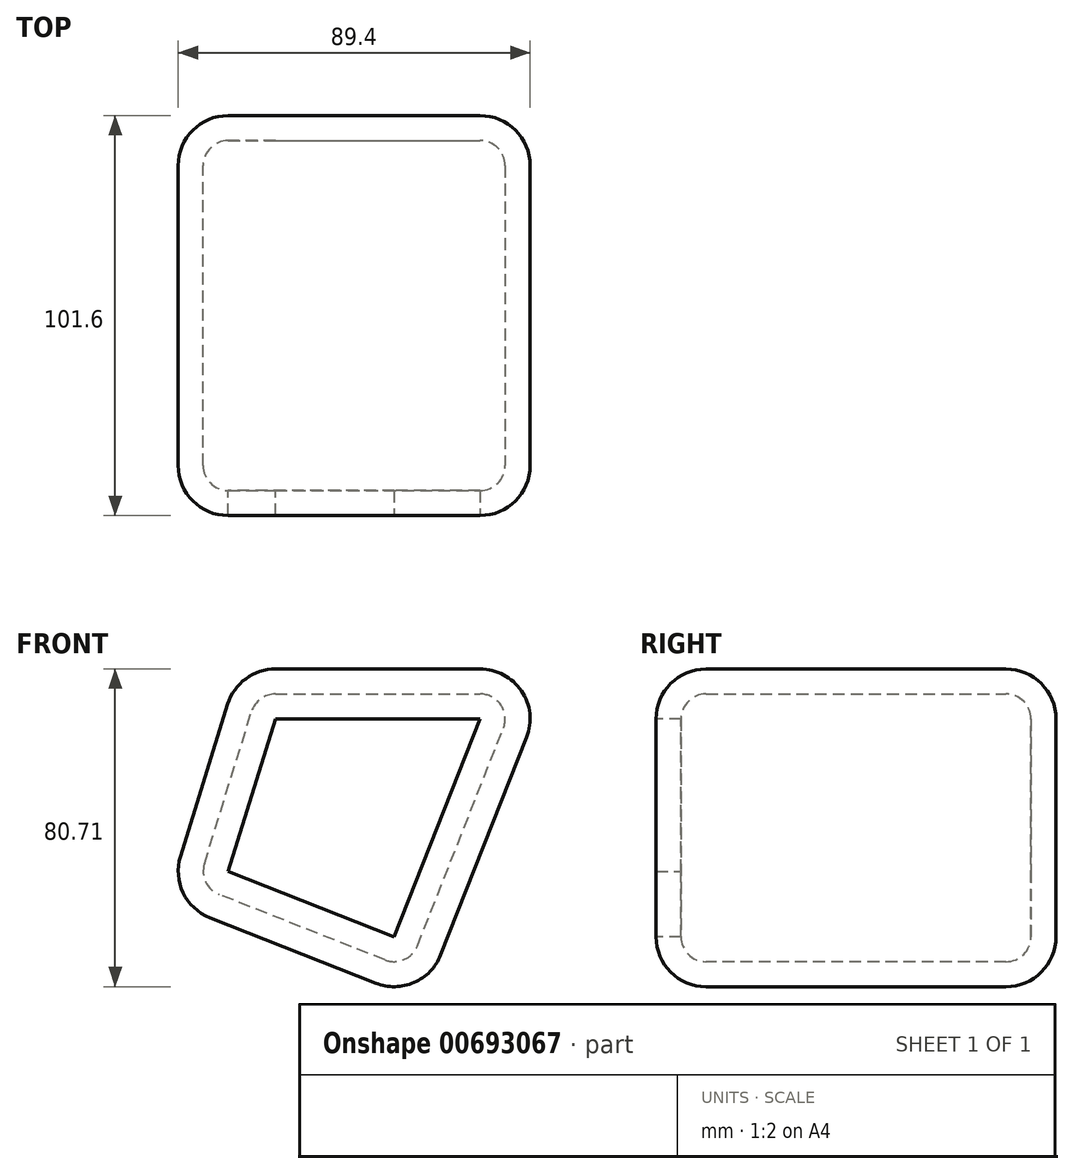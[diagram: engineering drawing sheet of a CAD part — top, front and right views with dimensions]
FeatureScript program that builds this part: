
annotation { "Feature Type Name" : "Feature", "Feature Type Description" : "" }
export const myFeature = defineFeature(function(context is Context, id is Id, definition is map)
    precondition{}
    {
        {
            var Q0;
            Q0=qCreatedBy(makeId("Front.planeOp"),FACE);
            var sketch = newSketch(context, id + "F0", { "sketchPlane" : qUnion([Q0])});
            skLineSegment(sketch, "E0", {"start": v(-44.02, 21.6) * mm, "end": v(36, 21.6) * mm});
            skLineSegment(sketch, "E1", {"start": v(36, 21.6) * mm, "end": v(36, 21.6) * mm});
            skLineSegment(sketch, "E2", {"start": v(2.64, -62.88) * mm, "end": v(36, 21.6) * mm});
            skLineSegment(sketch, "E3", {"start": v(2.64, -62.88) * mm, "end": v(-62.3, -37.23) * mm});
            skLineSegment(sketch, "E4", {"start": v(-62.3, -37.23) * mm, "end": v(-44.02, 21.6) * mm});
            skSolve(sketch);
        }
        {
            var Q0;
            Q0=makeQuery(id+"F0.imprint","IMPRINT",FACE,{"disambiguationData":[TD([[makeQuery(id+"F0.imprint","IMPRINT",EDGE,{"derivedFrom":sQuery(id+"F0.wireOp",EDGE,"E0")}),-1.0]])]});
            extrude(context, id + "F1", {"entities" : qUnion([Q0]), "endBound" : BoundingType.SYMMETRIC, "depth" : 101.6 * mm, "offsetDistance" : 25.4 * mm});
        }
        {
            var Q0;
            Q0=makeQuery(id+"F1.opExtrude","SWEPT_FACE",FACE,{"disambiguationData":[OSD([sQuery(id+"F0.wireOp",EDGE,"E0")])]});
            var Q1;
            Q1=makeQuery(id+"F1.opExtrude","CAP_FACE",FACE,{"disambiguationData":[OSD([sQuery(id+"F0.wireOp",EDGE,"E0"),sQuery(id+"F0.wireOp",EDGE,"E2"),sQuery(id+"F0.wireOp",EDGE,"E3"),sQuery(id+"F0.wireOp",EDGE,"E4")])],"isStart":false});
            var Q2;
            Q2=makeQuery(id+"F1.opExtrude","SWEPT_FACE",FACE,{"disambiguationData":[OSD([sQuery(id+"F0.wireOp",EDGE,"E2")])]});
            var Q3;
            Q3=makeQuery(id+"F1.opExtrude","CAP_FACE",FACE,{"disambiguationData":[OSD([sQuery(id+"F0.wireOp",EDGE,"E0"),sQuery(id+"F0.wireOp",EDGE,"E2"),sQuery(id+"F0.wireOp",EDGE,"E3"),sQuery(id+"F0.wireOp",EDGE,"E4")])],"isStart":true});
            var Q4;
            Q4=makeQuery(id+"F1.opExtrude","SWEPT_FACE",FACE,{"disambiguationData":[OSD([sQuery(id+"F0.wireOp",EDGE,"E3")])]});
            fillet(context, id + "F2", {"entities" : qUnion([Q0, Q1, Q2, Q3, Q4]), "radius" : 12.7 * mm, "tangentPropagation" : true, "allowEdgeOverflow" : false});
        }
        {
            var Q0;
            Q0=makeQuery(id+"F1.opExtrude","CAP_FACE",FACE,{"disambiguationData":[OSD([sQuery(id+"F0.wireOp",EDGE,"E0"),sQuery(id+"F0.wireOp",EDGE,"E2"),sQuery(id+"F0.wireOp",EDGE,"E3"),sQuery(id+"F0.wireOp",EDGE,"E4")])],"isStart":false});
            shell(context, id + "F3", {"entities" : qUnion([Q0]), "thickness" : 6.35 * mm});
        }
    });
